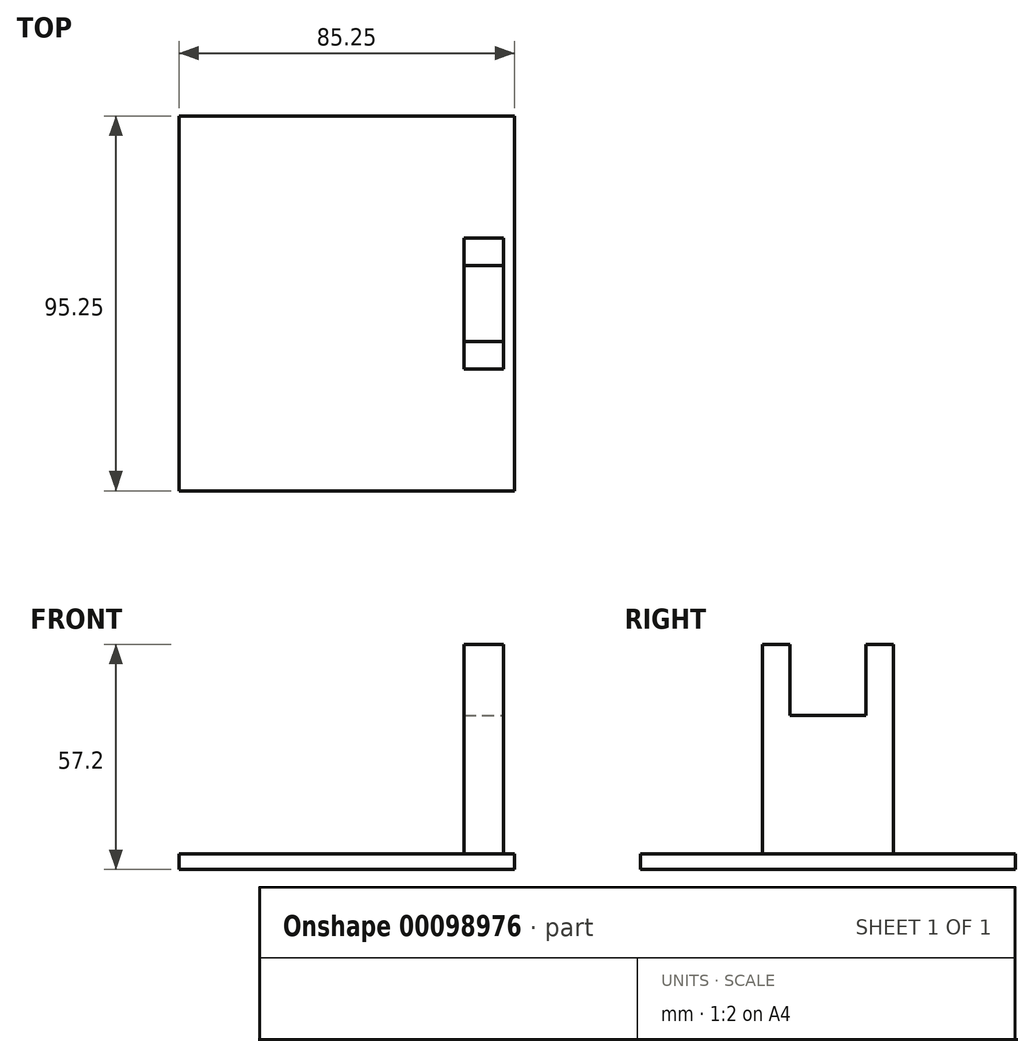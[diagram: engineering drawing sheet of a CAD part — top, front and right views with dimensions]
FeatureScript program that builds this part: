
annotation { "Feature Type Name" : "Feature", "Feature Type Description" : "" }
export const myFeature = defineFeature(function(context is Context, id is Id, definition is map)
    precondition{}
    {
        {
            var Q0;
            Q0=qCreatedBy(makeId("Top.planeOp"),FACE);
            var sketch = newSketch(context, id + "F0", { "sketchPlane" : qUnion([Q0])});
            skLineSegment(sketch, "E0.bottom", {"start": v(-47.98, 68.77) * mm, "end": v(37.27, 68.77) * mm});
            skLineSegment(sketch, "E0.top", {"start": v(-47.98, -26.48) * mm, "end": v(37.27, -26.48) * mm});
            skLineSegment(sketch, "E0.left", {"start": v(-47.98, 68.77) * mm, "end": v(-47.98, -26.48) * mm});
            skLineSegment(sketch, "E0.right", {"start": v(37.27, 68.77) * mm, "end": v(37.27, -26.48) * mm});
            skSolve(sketch);
        }
        {
            var Q0;
            Q0 = qSketchRegion(id + "F0", true);
            extrude(context, id + "F1", {"entities" : qUnion([Q0]), "depth" : 4 * mm});
        }
        {
            var Q0;
            Q0=makeQuery(id+"F1.opExtrude","CAP_FACE",FACE,{"disambiguationData":[OSD([sQuery(id+"F0.wireOp",EDGE,"E0.bottom"),sQuery(id+"F0.wireOp",EDGE,"E0.top"),sQuery(id+"F0.wireOp",EDGE,"E0.left"),sQuery(id+"F0.wireOp",EDGE,"E0.right")])],"isStart":false});
            var sketch = newSketch(context, id + "F2", { "sketchPlane" : qUnion([Q0])});
            skLineSegment(sketch, "E1", {"start": v(29.49, 79.07) * mm, "end": v(29.49, -42.17) * mm, "construction": true});
            skLineSegment(sketch, "E2", {"start": v(-57.42, 21.14) * mm, "end": v(73.55, 21.14) * mm, "construction": true});
            skSolve(sketch);
        }
        {
            var Q0;
            Q0=makeQuery(id+"F2.imprint","IMPRINT",FACE,{"disambiguationData":[TD([[makeQuery(id+"F2.imprint","IMPRINT",EDGE,{"derivedFrom":makeQuery(id+"F1.opExtrude","CAP_EDGE",EDGE,{"disambiguationData":[OSD([sQuery(id+"F0.wireOp",EDGE,"E0.bottom")])],"isStart":false})}),-1.0]])]});
            var sketch = newSketch(context, id + "F3", { "sketchPlane" : qUnion([Q0])});
            skLineSegment(sketch, "E3.bottom", {"start": v(24.49, 4.5) * mm, "end": v(34.49, 4.5) * mm});
            skLineSegment(sketch, "E3.top", {"start": v(24.49, 37.8) * mm, "end": v(34.49, 37.8) * mm});
            skLineSegment(sketch, "E3.left", {"start": v(24.49, 4.5) * mm, "end": v(24.49, 37.8) * mm});
            skLineSegment(sketch, "E3.right", {"start": v(34.49, 4.5) * mm, "end": v(34.49, 37.8) * mm});
            skSolve(sketch);
        }
        {
            var Q0;
            Q0 = qSketchRegion(id + "F3", true);
            extrude(context, id + "F4", {"entities" : qUnion([Q0]), "operationType" : NewBodyOperationType.ADD, "depth" : 53.2 * mm});
        }
        {
            var Q0;
            Q0=makeQuery(id+"F4.opExtrude","CAP_FACE",FACE,{"disambiguationData":[OSD([sQuery(id+"F3.wireOp",EDGE,"E3.bottom"),sQuery(id+"F3.wireOp",EDGE,"E3.top"),sQuery(id+"F3.wireOp",EDGE,"E3.left"),sQuery(id+"F3.wireOp",EDGE,"E3.right")])],"isStart":false});
            var sketch = newSketch(context, id + "F5", { "sketchPlane" : qUnion([Q0])});
            skLineSegment(sketch, "E4.bottom", {"start": v(24.49, 37.8) * mm, "end": v(34.49, 37.8) * mm});
            skLineSegment(sketch, "E4.top", {"start": v(24.49, 30.8) * mm, "end": v(34.49, 30.8) * mm});
            skLineSegment(sketch, "E4.left", {"start": v(24.49, 37.8) * mm, "end": v(24.49, 30.8) * mm});
            skLineSegment(sketch, "E4.right", {"start": v(34.49, 37.8) * mm, "end": v(34.49, 30.8) * mm});
            skLineSegment(sketch, "E5.bottom", {"start": v(34.49, 4.5) * mm, "end": v(24.49, 4.5) * mm});
            skLineSegment(sketch, "E5.top", {"start": v(34.49, 11.5) * mm, "end": v(24.49, 11.5) * mm});
            skLineSegment(sketch, "E5.left", {"start": v(34.49, 4.5) * mm, "end": v(34.49, 11.5) * mm});
            skLineSegment(sketch, "E5.right", {"start": v(24.49, 4.5) * mm, "end": v(24.49, 11.5) * mm});
            skSolve(sketch);
        }
        {
            var Q0;
            {var subQ0=sQuery(id+"F5.wireOp",EDGE,"E4.top");Q0=makeQuery(id+"F5.imprint","IMPRINT",FACE,{"disambiguationData":[TD([[makeQuery(id+"F5.imprint","IMPRINT",EDGE,{"derivedFrom":subQ0}),-1.0]])]});}
            var sketch = newSketch(context, id + "F6", { "sketchPlane" : qUnion([Q0])});
            skLineSegment(sketch, "E6.bottom", {"start": v(24.49, 30.8) * mm, "end": v(34.49, 30.8) * mm});
            skLineSegment(sketch, "E6.top", {"start": v(24.49, 11.5) * mm, "end": v(34.49, 11.5) * mm});
            skLineSegment(sketch, "E6.left", {"start": v(24.49, 30.8) * mm, "end": v(24.49, 11.5) * mm});
            skLineSegment(sketch, "E6.right", {"start": v(34.49, 30.8) * mm, "end": v(34.49, 11.5) * mm});
            skSolve(sketch);
        }
        {
            var Q0;
            Q0 = qSketchRegion(id + "F6", true);
            extrude(context, id + "F7", {"entities" : qUnion([Q0]), "operationType" : NewBodyOperationType.REMOVE, "oppositeDirection" : true, "depth" : 18 * mm});
        }
    });
